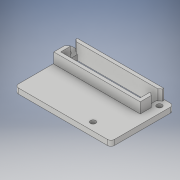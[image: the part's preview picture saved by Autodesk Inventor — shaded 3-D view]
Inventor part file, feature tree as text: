
AUTODESK INVENTOR PART (.ipt)
format: ipt  version: 2019 (Build 230136000, 136)  size: 183,296 bytes
history: native  units: mm
features: sketch x4, extrude x3, hole x1, projected_geometry x1
ambient origin geometry x8: Origin, YZ Plane, XZ Plane, XY Plane, X Axis, Y Axis, Z Axis, Center Point
bodies: Solid1 (feature_tree)
feature tree (9):
  extrude  "Extrusion1"  Depth=3.0mm TaperAngle=0.0deg
  hole  "Hole1"  [1 undecoded]
  extrude  "Extrusion6"  Depth=4.5mm
  extrude  "Extrusion7"  Depth=36.0mm
  sketch  "Sketch1"  dims[d0=60.0mm d2=3.0mm d3=0.0mm]
  sketch  "Sketch7"  dims[d35=3.0mm d36=6.0mm d37=4.0mm d38=2.0mm d39=90.0deg d40=10.25mm d41=0.0mm d42=27.0mm]
  projected_geometry  "Projected Loop4"
  sketch  "Sketch8"  dims[d43=52.5mm d44=4.5mm]
  sketch  "Sketch9"  dims[d45=11.0mm d47=36.0mm d48=9.0mm d49=5.0mm d50=3.75mm d58=2.0mm d60=2.0mm d68=2.0mm d69=6.0mm d70=0.0mm d73=9.5mm d74=45.5mm d75=7.0mm d76=7.0mm d77=2.5mm d78=2.0mm d81=2.0mm d82=9.5mm d83=2.0mm d84=49.5mm d85=49.5mm d86=49.5mm d87=2.0mm d88=20.25mm d89=0.0mm]
note: 1 required parameter value undecoded (feature->parameter linkage not recoverable at this tier; creation-order binding heuristic only, values carry confidence <= 0.55)
